# Revit family: 10-HC_RAS_HCL_TOSHIBA_TCTC_2MU2AVG_10-18
name_source: partatom
category: Mechanical Equipment
revit_build: Autodesk Revit 2017 (Build: 20160225_1515(x64)
units: mm (PartAtom-declared; Revit-internal decimal feet)

## family parameters
Always vertical = Yes
Cut with Voids When Loaded = No
OmniClass Number = 23.75.00.00
OmniClass Title = Climate Control (HVAC)
Part Type = Normal
Room Calculation Point = No
Round Connector Dimension = Use Diameter
Shared = No
Work Plane-Based = No

## types (3) — shared parameters
Article Description = Multi R32
Compressor Type = Hermetic DC Twin rotary compressor
Content Supplier URL = www.hcltech.com
Custom = No
Depth (mm) = 300 mm
Description = Multi R32
Drain pipe = -
Duct diameters = -
EMCS = 4
ETIM Article Class = EC001213
Energy class = A++ / A++
Frequency (Hz) = 50Hz
Height (mm) = 630 mm  [stored 2.06693 ft]
Hydronic Return Diameter (mm) = 10 mm  [stored 0.0328084 ft]
Hydronic Supply Diameter (mm) = 6 mm  [stored 0.019685 ft]
MEPcontent Class = HEATPUMP
MOCP (A) = 15
Manufacturer = Toshiba
Manufacturer URL = https://www.toshiba-carrier.co.jp
Operating range - Cooling (°C) = -10 - 46
Operating range - Heating (°C) = -20 - 24
Product Line = TCTC
Red = Colour RGB-250 000 000
Refrigerant information = R32
URL = https://www.toshiba-carrier.co.jp
Voltage (V) = 220-240V
White = Colour RGB-255 255 255
Width (mm) = 799 mm  [stored 2.62139 ft]

## per-type parameters (varying)
| type | Airflow m3/h- Cooling/Heating | Compressor detail - Motor output  (kW) | Pdesigh | Power consumption-Cooling (Kw) | Power consumption-Heating (Kw) | Rated Capacity kW - Cooling/Heating | Rated Power Consumption kW - Cooling/Heating | Rated efficiency - EER / COP | Running current-Cooling (A) | Running current-Heating (A) | Seasonal efficiency - SEER  / SCOP | Sound pressure dB(A) Cooling/Heating- High | Starting current | Weight (Kg) |
| RAS-2M10U2AVG-E | 1863 / 1863 | 1050 | 3.3 / 2.7 | 750 | 810 | 3.3 / 4.0 | 750 / 810 | 4.40 / 4.94 | 3.93/3.75/3.57 | 4.17/4.02/3.85 | 6.73 / 4.60 | 45 / 46 | 4.17 | 42 |
| RAS-2M14U2AVG-E | 1863 / 1863 | 1050 | 4.0 / 3.1 | 920 | 890 | 4.0 / 4.4 | 920 / 890 | 4.35 / 4.94 | 4.55/4.35/4.15 | 4.40/4.20/4.05 | 6.73 / 4.60 | 45 / 46 | 4.55 | 43 |
| RAS-2M18U2AVG-E | 2107 / 2038 | 1320 | 5.2 / 3.2 | 1340 | 1190 | 5.2 / 5.6 | 1340 / 1190 | 3.88 / 4.71 | 6.43/6.15/5.90 | 5.73/5.48/5.26 | 6.90 / 4.60 | 45 / 50 | 6.43 | 45 |

note: column(s) folded — value = type name in every type: Article Type, Manufacturer Art. No., Model

note: [stored X ft] marks values corroborated as IEEE doubles in the binary element streams (Revit-internal decimal feet)

## geometry (parser evidence)
native form markers: Sweep x7
no freeform markers — native parametric forms only
